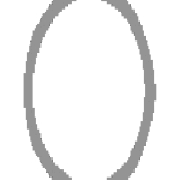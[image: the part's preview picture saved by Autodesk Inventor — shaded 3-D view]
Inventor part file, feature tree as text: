
AUTODESK INVENTOR PART (.ipt)
format: ipt  version: 2021 (Build 250183000, 183)  size: 110,592 bytes
history: native  units: in
note: dims shown in document units (in); Inventor stores cm internally (conversion verified against a paired STEP export)
features: other x4, sketch x3, plane x1
ambient origin geometry x8: Origin, YZ Plane, XZ Plane, XY Plane, X Axis, Y Axis, Z Axis, Center Point
bodies: Solid1 (feature_tree), Body (feature_tree)
feature tree (8):
  other  "Driven Length"
  other  "Frame Generator"
  other  "Start Plane"
  other  "End Plane"
  sketch  "Sketch"  dims[d2=11.5in d4=-0.0in d5=11.5in d6=0.12in d7=0.0in d8=90.0deg d9=11.5in]
  sketch  "Sketch2"  dims[d0=1.0in]
  plane  "Work Plane3"
  sketch  "Sketch3"  dims[d1=0.065in]
